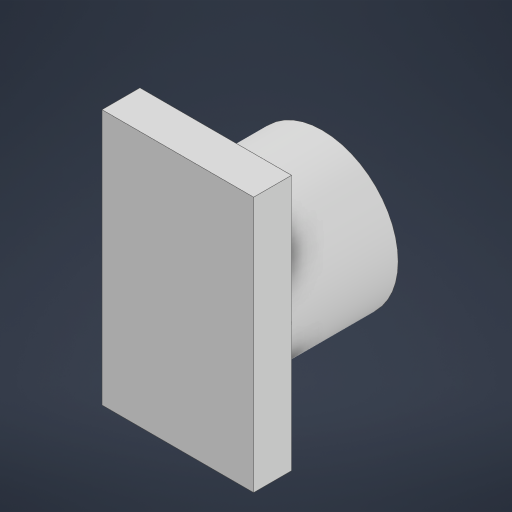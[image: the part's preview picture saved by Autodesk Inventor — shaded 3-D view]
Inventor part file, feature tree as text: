
AUTODESK INVENTOR PART (.ipt)
format: ipt  version: 2023 (Build 270158000, 158)  size: 180,224 bytes
history: native  units: in
note: dims shown in document units (in); Inventor stores cm internally (conversion verified against a paired STEP export)
features: extrude x2, sketch x1, chamfer x1
ambient origin geometry x8: Origin, YZ Plane, XZ Plane, XY Plane, X Axis, Y Axis, Z Axis, Center Point
bodies: Solid1 (feature_tree)
feature tree (4):
  sketch  "Sketch1"  dims[d0=0.126in d1=0.2126in d2=0.0315in d3=0.0in d4=0.0984in d5=0.0in d6=0.0315in d7=0.0098in d8=15.0deg d9=0.126in d10=0.0157in d11=0.0197in d12=0.0344in d13=0.0344in]
  extrude  "Extrusion1"  Depth=0.2126in
  extrude  "Extrusion2"  Depth=0.0315in TaperAngle=0.0deg
  chamfer  "Chamfer1"  Distance=0.0984in
